# Revit family: Bathroom_Accessory-Towel_Ring-Kohler-Kelston-13507
name_source: partatom
category: Specialty Equipment
units: mm (PartAtom-declared; Revit-internal decimal feet)

## family parameters
Cut with Voids When Loaded = No
Host = Face
OmniClass Number = 23.40.20.21.27
OmniClass Title = Towel Bars
Part Type = Normal
Room Calculation Point = No
Round Connector Dimension = Use Diameter
Shared = No

## types (1)
- Chrome-Polished_Chrome-CP
    Assembly Code = C1030200
    Default Elevation = 0' - 0"
    Description = Kelston(TM) towel ring
    Finish = Chrome-Kohler-CP-Polished_Chrome
    Height = 0' - 8 3/16"
    Length = 0' - 3 7/8"
    Manufacturer = Kohler
    Model = K-13507
    Product Documentation Link = http://www.us.kohler.com
    Product Page URL = http://www.us.kohler.com
    Product data url = https://bimobject.com
    URL = http://www.us.kohler.com
    Width = 0' - 7 3/16"

## geometry (parser evidence)
native form markers: Sweep x4
no freeform markers — native parametric forms only
